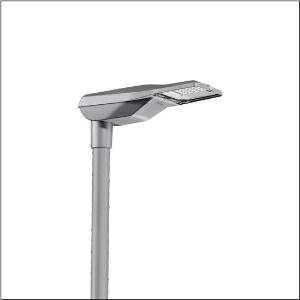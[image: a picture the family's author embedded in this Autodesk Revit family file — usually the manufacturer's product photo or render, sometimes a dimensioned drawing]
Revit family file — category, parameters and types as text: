
# Revit family: streetlight_sl_21_iq_micro___st1_0a_5xe1d31g08cb_12bc
name_source: partatom
category: Lighting Fixtures
units: mm (PartAtom-declared; Revit-internal decimal feet)

## family parameters
Cut with Voids When Loaded = No
Host = Face
Light Source = No
Part Type = Normal
Room Calculation Point = No
Round Connector Dimension = Use Diameter
Shared = No

## types (1)
- --- (1 x LED, 2870 lm, 19.4 W, 3000K)
    Apparent Load = 19 VA
    CIE Flux Codes = 37 72 97 100 100
    Color Rendering = 70
    Color Temperature = 3000K
    Default Elevation = 1800 mm
    Description = Streetlight SL 21 iQ micro, mast luminaire, primary light control with lens, of PMMA, primary optical cover: cover, of toughened safety glass, transparent, light distribution: ST1.0a, light emission: direct distribution, primary light characteristic: asymmetric, installation type: post-top, side-entry, LED, High Power LED, rated luminous flux: 2.870lm, luminous efficacy: 148lm/W, light colour: 730, colour temperature: 3000K, control: Street-Remote, Auto-Match, Temp-Guard, Lumen-Switch, Night-Set, Smart-Wire, Light-Fading, Desk-Remote (wireless, voltage-free reading and setting of iQ features in the workshop via application-optimized NFC function/RFID function), optimised constant luminous flux control (CLO 2.0), pre-setting: linear dimming characteristic, mains connection: 220..240V, AC, 50/60Hz, start of lifetime: 19W, end of service life: 20W, reduction: 10W, luminaire housing, of diecast aluminium, powder-coated, Siteco® metallic grey (DB 702S), corrosivity category C5 mid according to DIN EN ISO 12944, please order mast flange separately, inclination adjustable: 0°, 5°, 10°, 15°, sealing non-destructively replaceable, multi-level sealing system, length: 528mm, width: 235mm, height: 110mm, mast flange for spigot size: 42mm (side-entry): 5XC10008XM4, 60/48mm (side-entry/post-top): 5XC10108XM2, 76/60mm (side-entry/post-top): 5XC10108XM1, protection rating (complete): IP66, insulation class (complete): insulation class II (safety insulation), certification: CE, ENEC, ENEC+, VDE, impact resistance: IK09, permissible operating ambient temperature for outdoor applications: -40..+50°C, standard-compliant lighting for roads and squares, packaging unit: 1 piece

Light Distribution: ST1.0a
    Height = 110 mm
    Lamp = 1 x LED
    Lamp Light Flux = 2870 lm
    Lamp Power = 19.4 W
    Lamp count = 1
    Length = 528 mm
    Luminous efficacy = 148 lm/W
    Manufacturer = Siteco
    ModVariant = No
    Model = 5XE1D31G08CB
    Number of Poles = 1
    OnlyDefault = Yes
    Power Factor = 1
    Product Name = Streetlight SL 21 iQ micro | ST1.0a
    Product group = mast luminaire | pylon top
    ProductGroupID = 6100
    Protection Class = Protection class II
    Protection Degree = IP 66
    RLX_Detail_Level = 1
    RLX_Emergency_Light_Flux = 0 lm
    RLX_Emergency_Type = 0
    RLX_Emergency_Type_DB = No
    RlxData = <blob elided: 98869 chars, md5=b9a28a87>
    Socket = socket
    Standby Power = 0 W
    System Light Flux = 2870 lm
    System Power = 19 W
    Type Comments = factory setting: luminous flux: 100 % | dim-lin: 254 | 387 mA
    Type Image = l_1006881.jpg
    URL = http://relux.com
    VarID = @adj_109055
    Voltage = 0 V
    Weight = 0.00 kg
    Width = 235 mm

## geometry (parser evidence)
native form markers: Blend x4, Sweep x12
no freeform markers — native parametric forms only
